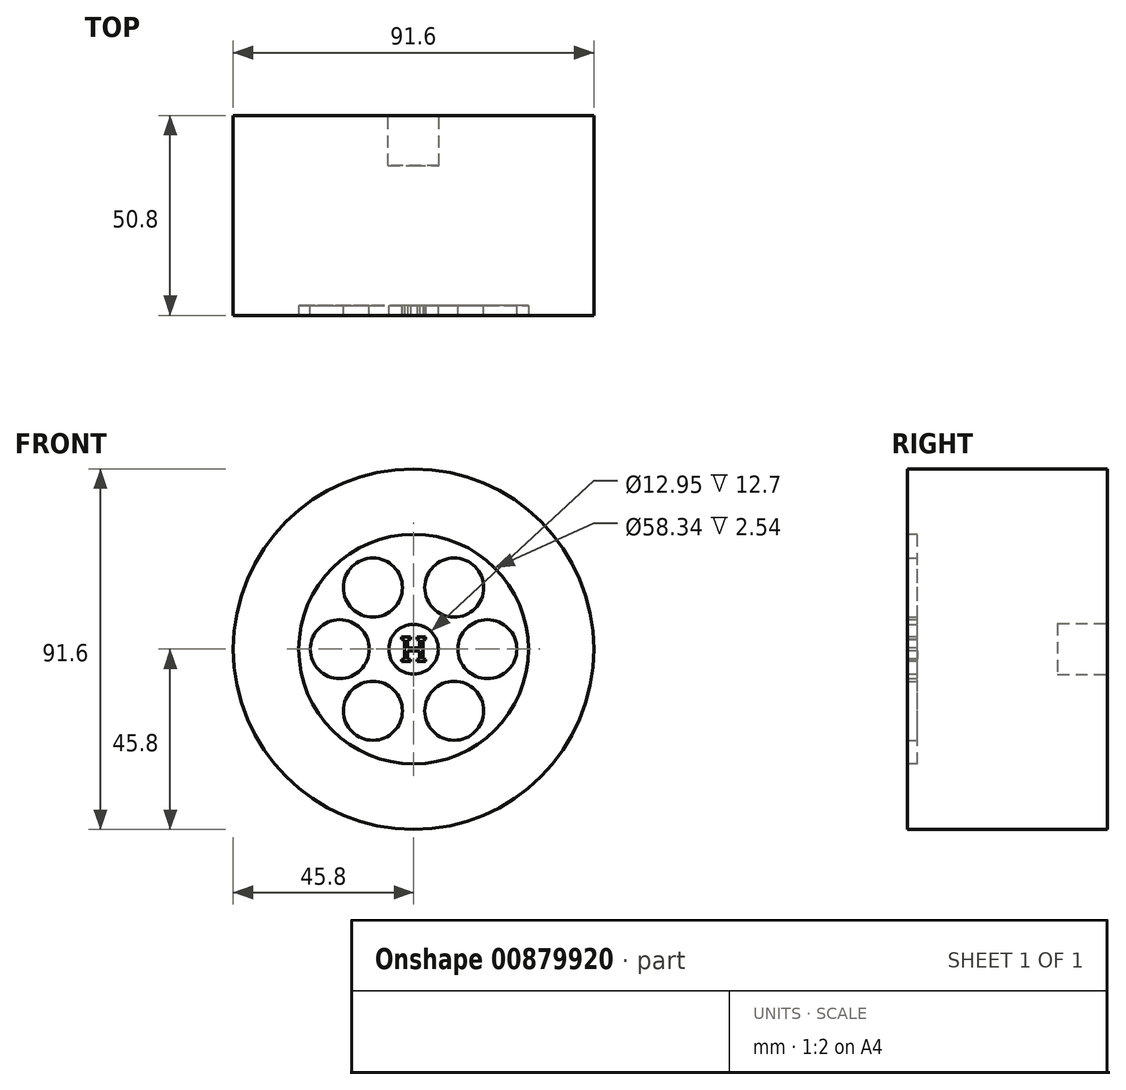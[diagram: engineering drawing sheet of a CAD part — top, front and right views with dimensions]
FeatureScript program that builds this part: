
annotation { "Feature Type Name" : "Feature", "Feature Type Description" : "" }
export const myFeature = defineFeature(function(context is Context, id is Id, definition is map)
    precondition{}
    {
        {
            var Q0;
            Q0=qCreatedBy(makeId("Front.planeOp"),FACE);
            var sketch = newSketch(context, id + "F0", { "sketchPlane" : qUnion([Q0])});
            skCircle(sketch, "E0", {"center": v(0, 0) * mm, "radius": 45.8 * mm});
            skSolve(sketch);
        }
        {
            var Q0;
            Q0 = qSketchRegion(id + "F0", true);
            extrude(context, id + "F1", {"entities" : qUnion([Q0]), "depth" : 50.8 * mm, "offsetDistance" : 25.4 * mm});
        }
        {
            var Q0;
            Q0=makeQuery(id+"F1.opExtrude","CAP_FACE",FACE,{"disambiguationData":[OSD([sQuery(id+"F0.wireOp",EDGE,"E0")])],"isStart":true});
            var sketch = newSketch(context, id + "F2", { "sketchPlane" : qUnion([Q0])});
            skCircle(sketch, "E1", {"center": v(0, 0) * mm, "radius": 6.48 * mm});
            skSolve(sketch);
        }
        {
            var Q0;
            Q0 = qSketchRegion(id + "F2", true);
            extrude(context, id + "F3", {"entities" : qUnion([Q0]), "operationType" : NewBodyOperationType.REMOVE, "oppositeDirection" : true, "depth" : 12.7 * mm, "offsetDistance" : 25.4 * mm});
        }
        {
            var Q0;
            Q0=makeQuery(id+"F1.opExtrude","CAP_FACE",FACE,{"disambiguationData":[OSD([sQuery(id+"F0.wireOp",EDGE,"E0")])],"isStart":false});
            var sketch = newSketch(context, id + "F4", { "sketchPlane" : qUnion([Q0])});
            skCircle(sketch, "E2", {"center": v(0, 0) * mm, "radius": 29.17 * mm});
            skSolve(sketch);
        }
        {
            var Q0;
            Q0 = qSketchRegion(id + "F4", true);
            extrude(context, id + "F5", {"entities" : qUnion([Q0]), "operationType" : NewBodyOperationType.REMOVE, "oppositeDirection" : true, "depth" : 2.54 * mm, "offsetDistance" : 25.4 * mm});
        }
        {
            var Q0;
            Q0=makeQuery(id+"F5.boolean.opBoolean","COPY",FACE,{"derivedFrom":makeQuery(id+"F5.opExtrude","CAP_FACE",FACE,{"disambiguationData":[OSD([sQuery(id+"F4.wireOp",EDGE,"E2")])],"isStart":false})});
            var sketch = newSketch(context, id + "F6", { "sketchPlane" : qUnion([Q0])});
            skCircle(sketch, "E3", {"center": v(0, 0) * mm, "radius": 6.3 * mm});
            skSolve(sketch);
        }
        {
            var Q0;
            Q0 = qSketchRegion(id + "F6", true);
            extrude(context, id + "F7", {"entities" : qUnion([Q0]), "operationType" : NewBodyOperationType.ADD, "depth" : 2.54 * mm, "offsetDistance" : 25.4 * mm});
        }
        {
            var Q0;
            Q0=makeQuery(id+"F7.opExtrude","CAP_FACE",FACE,{"disambiguationData":[OSD([sQuery(id+"F6.wireOp",EDGE,"E3")])],"isStart":false});
            var sketch = newSketch(context, id + "F8", { "sketchPlane" : qUnion([Q0])});
            skText(sketch, "E4", { "text": "H", "fontName": "RobotoSlab-Regular.ttf"});
            const initialGuessF8  = {"E4": [-0.00331, -0.00314, 1, 0, 0.00628]};
            skSetInitialGuess(sketch, initialGuessF8);
            skSolve(sketch);
        }
        {
            var Q0;
            Q0 = qSketchRegion(id + "F8", true);
            extrude(context, id + "F9", {"entities" : qUnion([Q0]), "operationType" : NewBodyOperationType.REMOVE, "oppositeDirection" : true, "depth" : 2.54 * mm, "offsetDistance" : 25.4 * mm});
        }
        {
            var Q0;
            Q0=makeQuery(id+"F5.boolean.opBoolean","COPY",FACE,{"derivedFrom":makeQuery(id+"F5.opExtrude","CAP_FACE",FACE,{"disambiguationData":[OSD([sQuery(id+"F4.wireOp",EDGE,"E2")])],"isStart":false})});
            var sketch = newSketch(context, id + "F10", { "sketchPlane" : qUnion([Q0])});
            skCircle(sketch, "E5", {"center": v(-10.33, -15.66) * mm, "radius": 7.5 * mm});
            skCircle(sketch, "E6", {"center": v(-18.76, 0) * mm, "radius": 7.5 * mm});
            skCircle(sketch, "E7", {"center": v(-10.33, 15.66) * mm, "radius": 7.5 * mm});
            skCircle(sketch, "E8", {"center": v(10.33, 15.66) * mm, "radius": 7.5 * mm});
            skCircle(sketch, "E9", {"center": v(18.76, 0) * mm, "radius": 7.5 * mm});
            skCircle(sketch, "E10", {"center": v(10.33, -15.66) * mm, "radius": 7.5 * mm});
            skSolve(sketch);
        }
        {
            var Q0;
            Q0 = qSketchRegion(id + "F10", true);
            extrude(context, id + "F11", {"entities" : qUnion([Q0]), "operationType" : NewBodyOperationType.ADD, "depth" : 2.54 * mm, "offsetDistance" : 25.4 * mm});
        }
    });
